# Revit family: Rheem Mains Pressure Vitreous Enamel HWC
name_source: partatom
category: Plumbing Fixtures
units: mm (PartAtom-declared; Revit-internal decimal feet)

## family parameters
Always vertical = Yes
Cut with Voids When Loaded = No
Maintain Annotation Orientation = No
OmniClass Number = 23.45.00.00
OmniClass Title = Sanitary, Laundry, and Cleaning Equipment
Part Type = Normal
Room Calculation Point = No
Round Connector Dimension = Use Diameter
Shared = No
Work Plane-Based = No

## types (21) — shared parameters
Connection E - Angle = 22.50°
Manufacturer = Rheem
Top Connection Size = 75 mm
URL = https://rheem.co.nz
zero-valued in all types: Default Elevation

## per-type parameters (varying)
| type | A - Height | Approx. Storage Capacity | B - Width | Boost Capacity (Twin Element) | C - Height | Connection - D | Connection D | Connection E | Connection Length | D - Height | E - Height | Element Rating (@230V) | F - Height | H - Angle | Model | Top Connection Placement | Type Comments |
| Dual Element (simultaneous) Indoor - 300L - 31230033 | 1815 mm  [stored 5.95472 ft] | 300 m³ | 580 mm  [stored 1.90289 ft] | 50 m³ | 120 mm  [stored 0.393701 ft] | 300 mm  [stored 0.984252 ft] | Yes | Yes | 300 mm  [stored 0.984252 ft] | 65 mm  [stored 0.213255 ft] | 162 mm  [stored 0.531496 ft] | 5000 W | 1126 mm  [stored 3.69423 ft] | 45.00° | 31230033 | 145 mm  [stored 0.475722 ft] | Dual Element (simultaneous) Indoor |
| Dual Element (simultaneous) Indoor - 300L - 31230055 | 1815 mm  [stored 5.95472 ft] | 300 m³ | 580 mm  [stored 1.90289 ft] | 50 m³ | 120 mm  [stored 0.393701 ft] | 300 mm  [stored 0.984252 ft] | Yes | Yes | 300 mm  [stored 0.984252 ft] | 65 mm  [stored 0.213255 ft] | 162 mm  [stored 0.531496 ft] | 5000 W | 1126 mm  [stored 3.69423 ft] | 45.00° | 31230055 | 145 mm  [stored 0.475722 ft] | Dual Element (simultaneous) Indoor |
| Twin Element (non-simultaneous) Indoor - 300L - 31230025 | 1815 mm  [stored 5.95472 ft] | 300 m³ | 580 mm  [stored 1.90289 ft] | 50 m³ | 120 mm  [stored 0.393701 ft] | 300 mm  [stored 0.984252 ft] | Yes | Yes | 300 mm  [stored 0.984252 ft] | 65 mm  [stored 0.213255 ft] | 162 mm  [stored 0.531496 ft] | 3000 W | 1126 mm  [stored 3.69423 ft] | 45.00° | 31230025 | 145 mm  [stored 0.475722 ft] | Twin Element (non-simultaneous) Indoor |
| Optima Twin Element (non-simultaneous) Outdoor/Indoor - 400L - 492400G8 | 1840 mm  [stored 6.03675 ft] | 400 m³ | 690 mm  [stored 2.26378 ft] | 90 m³ | 120 mm  [stored 0.393701 ft] | 355 mm | Yes | No | 355 mm | 105 mm  [stored 0.344488 ft] | 0 mm  [stored 0 ft] | 4800 W | 1323 mm  [stored 4.34055 ft] | 97.00° | 492400G8 | 173 mm | Optima Twin Element (non-simultaneous) Outdoor/Indoor |
| Optima Twin Element (non-simultaneous) Outdoor/Indoor - 300L - 91330025 | 1820 mm | 300 m³ | 580 mm  [stored 1.90289 ft] | 47 m³ | 120 mm  [stored 0.393701 ft] | 300 mm  [stored 0.984252 ft] | No | No | 300 mm  [stored 0.984252 ft] | 0 mm  [stored 0 ft] | 0 mm  [stored 0 ft] | 5000 W | 1298 mm  [stored 4.25853 ft] | 36.00° | 91330025 | 145 mm  [stored 0.475722 ft] | Optima Twin Element (non-simultaneous) Outdoor/Indoor |
| Single Element Indoor - 300L - 31230015 | 1815 mm  [stored 5.95472 ft] | 300 m³ | 580 mm  [stored 1.90289 ft] | 50 m³ | 120 mm  [stored 0.393701 ft] | 300 mm  [stored 0.984252 ft] | Yes | Yes | 300 mm  [stored 0.984252 ft] | 65 mm  [stored 0.213255 ft] | 162 mm  [stored 0.531496 ft] | 3000 W | 1126 mm  [stored 3.69423 ft] | 45.00° | 31230015 | 145 mm  [stored 0.475722 ft] | Single Element Indoor |
| Single Element Indoor - 250L - 31225025 | 1555 mm  [stored 5.10171 ft] | 250 m³ | 580 mm  [stored 1.90289 ft] | 50 m³ | 120 mm  [stored 0.393701 ft] | 300 mm  [stored 0.984252 ft] | Yes | No | 300 mm  [stored 0.984252 ft] | 65 mm  [stored 0.213255 ft] | 0 mm  [stored 0 ft] | 3000 W | 1126 mm  [stored 3.69423 ft] | 45.00° | 31225025 | 145 mm  [stored 0.475722 ft] | Single Element Indoor |
| Single Element Indoor - 250L - 31225015 | 1555 mm  [stored 5.10171 ft] | 250 m³ | 580 mm  [stored 1.90289 ft] | 0 m³ | 120 mm  [stored 0.393701 ft] | 300 mm  [stored 0.984252 ft] | Yes | No | 300 mm  [stored 0.984252 ft] | 65 mm  [stored 0.213255 ft] | 0 mm  [stored 0 ft] | 3000 W | 0 mm  [stored 0 ft] | 45.00° | 31225015 | 145 mm  [stored 0.475722 ft] | Single Element Indoor |
| Single Element Indoor - 180L - 32218015 | 1165 mm  [stored 3.82218 ft] | 180 m³ | 580 mm  [stored 1.90289 ft] | 0 m³ | 120 mm  [stored 0.393701 ft] | 300 mm  [stored 0.984252 ft] | Yes | No | 300 mm  [stored 0.984252 ft] | 65 mm  [stored 0.213255 ft] | 0 mm  [stored 0 ft] | 3000 W | 0 mm  [stored 0 ft] | 45.00° | 32218015 | 145 mm  [stored 0.475722 ft] | Single Element Indoor |
| Optima Outdoor/Indoor - 180L - 91318015 | 1710 mm  [stored 5.61024 ft] | 180 m³ | 490 mm  [stored 1.60761 ft] | 0 m³ | 120 mm  [stored 0.393701 ft] | 255 mm  [stored 0.836614 ft] | No | No | 255 mm  [stored 0.836614 ft] | 0 mm  [stored 0 ft] | 0 mm  [stored 0 ft] | 3000 W | 0 mm  [stored 0 ft] | 36.00° | 91318015 | 123 mm | Optima Outdoor/Indoor |
| Twin Element (non-simultaneous) Indoor - 180L - 31218025 | 1710 mm  [stored 5.61024 ft] | 180 m³ | 490 mm  [stored 1.60761 ft] | 45 m³ | 120 mm  [stored 0.393701 ft] | 255 mm  [stored 0.836614 ft] | Yes | No | 255 mm  [stored 0.836614 ft] | 65 mm  [stored 0.213255 ft] | 0 mm  [stored 0 ft] | 3000 W | 1182 mm  [stored 3.87795 ft] | 45.00° | 31218025 | 123 mm | Twin Element (non-simultaneous) Indoor |
| Single Element Indoor - 180L - 31218015 | 1710 mm  [stored 5.61024 ft] | 180 m³ | 490 mm  [stored 1.60761 ft] | 0 m³ | 120 mm  [stored 0.393701 ft] | 255 mm  [stored 0.836614 ft] | Yes | No | 255 mm  [stored 0.836614 ft] | 65 mm  [stored 0.213255 ft] | 0 mm  [stored 0 ft] | 3000 W | 0 mm  [stored 0 ft] | 45.00° | 31218015 | 123 mm | Single Element Indoor |
| Single Element Indoor - 180L - 31218013 | 1710 mm  [stored 5.61024 ft] | 180 m³ | 490 mm  [stored 1.60761 ft] | 0 m³ | 120 mm  [stored 0.393701 ft] | 255 mm  [stored 0.836614 ft] | Yes | No | 255 mm  [stored 0.836614 ft] | 65 mm  [stored 0.213255 ft] | 0 mm  [stored 0 ft] | 2000 W | 0 mm  [stored 0 ft] | 45.00° | 31218013 | 123 mm | Single Element Indoor |
| Single Element Indoor - 135L - 31213515 | 1325 mm  [stored 4.34711 ft] | 135 m³ | 490 mm  [stored 1.60761 ft] | 0 m³ | 120 mm  [stored 0.393701 ft] | 255 mm  [stored 0.836614 ft] | Yes | No | 255 mm  [stored 0.836614 ft] | 65 mm  [stored 0.213255 ft] | 0 mm  [stored 0 ft] | 3000 W | 0 mm  [stored 0 ft] | 45.00° | 31213515 | 123 mm | Single Element Indoor |
| Single Element Indoor - 135L - 31213513 | 1325 mm  [stored 4.34711 ft] | 135 m³ | 490 mm  [stored 1.60761 ft] | 0 m³ | 120 mm  [stored 0.393701 ft] | 255 mm  [stored 0.836614 ft] | Yes | No | 255 mm  [stored 0.836614 ft] | 65 mm  [stored 0.213255 ft] | 0 mm  [stored 0 ft] | 2000 W | 0 mm  [stored 0 ft] | 45.00° | 31213513 | 123 mm | Single Element Indoor |
| Single Element Indoor - 90L - 31209013 | 925 mm  [stored 3.03478 ft] | 90 m³ | 490 mm  [stored 1.60761 ft] | 0 m³ | 120 mm  [stored 0.393701 ft] | 255 mm  [stored 0.836614 ft] | Yes | No | 255 mm  [stored 0.836614 ft] | 65 mm  [stored 0.213255 ft] | 0 mm  [stored 0 ft] | 3000 W | 0 mm  [stored 0 ft] | 45.00° | 31209013 | 123 mm | Single Element Indoor |
| Single Element Indoor - 90L - 31209015 | 925 mm  [stored 3.03478 ft] | 90 m³ | 490 mm  [stored 1.60761 ft] | 0 m³ | 120 mm  [stored 0.393701 ft] | 255 mm  [stored 0.836614 ft] | Yes | No | 255 mm  [stored 0.836614 ft] | 65 mm  [stored 0.213255 ft] | 0 mm  [stored 0 ft] | 2000 W | 0 mm  [stored 0 ft] | 45.00° | 31209015 | 123 mm | Single Element Indoor |
| Single Element Indoor - 45L - 31204513 | 525 mm | 45 m³ | 490 mm  [stored 1.60761 ft] | 0 m³ | 116 mm  [stored 0.380577 ft] | 255 mm  [stored 0.836614 ft] | Yes | No | 255 mm  [stored 0.836614 ft] | 65 mm  [stored 0.213255 ft] | 0 mm  [stored 0 ft] | 3000 W | 0 mm  [stored 0 ft] | 45.00° | 31204513 | 123 mm | Single Element Indoor |
| Single Element Indoor - 45L - 31204515 | 525 mm | 45 m³ | 490 mm  [stored 1.60761 ft] | 0 m³ | 116 mm  [stored 0.380577 ft] | 255 mm  [stored 0.836614 ft] | Yes | No | 255 mm  [stored 0.836614 ft] | 65 mm  [stored 0.213255 ft] | 0 mm  [stored 0 ft] | 2000 W | 0 mm  [stored 0 ft] | 45.00° | 31204515 | 123 mm | Single Element Indoor |
| Single Element Indoor - 25L - 31202519V | 398 mm  [stored 1.30577 ft] | 25 m³ | 400 mm  [stored 1.31234 ft] | 0 m³ | 116 mm  [stored 0.380577 ft] | 210 mm  [stored 0.688976 ft] | Yes | No | 210 mm  [stored 0.688976 ft] | 32 mm  [stored 0.104987 ft] | 0 mm  [stored 0 ft] | 2000 W | 0 mm  [stored 0 ft] | 45.00° | 31202519V | 100 mm  [stored 0.328084 ft] | Single Element Indoor |
| Single Element Indoor - 135L - 32213515 | 935 mm | 135 m³ | 580 mm  [stored 1.90289 ft] | 0 m³ | 120 mm  [stored 0.393701 ft] | 300 mm  [stored 0.984252 ft] | Yes | No | 300 mm  [stored 0.984252 ft] | 65 mm  [stored 0.213255 ft] | 0 mm  [stored 0 ft] | 3000 W | 0 mm  [stored 0 ft] | 45.00° | 32213515 | 145 mm  [stored 0.475722 ft] | Single Element Indoor |

note: [stored X ft] marks values corroborated as IEEE doubles in the binary element streams (Revit-internal decimal feet)

## geometry (parser evidence)
native form markers: Sweep x1
no freeform markers — native parametric forms only
